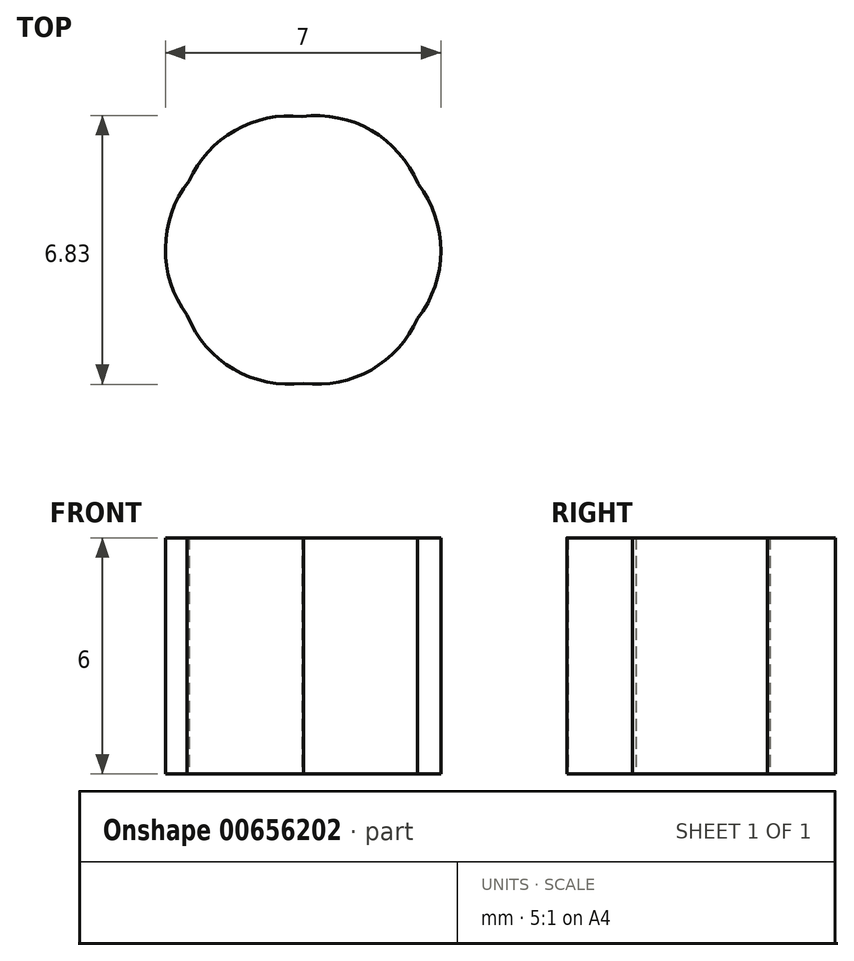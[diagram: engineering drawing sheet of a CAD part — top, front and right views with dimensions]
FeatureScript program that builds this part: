
annotation { "Feature Type Name" : "Feature", "Feature Type Description" : "" }
export const myFeature = defineFeature(function(context is Context, id is Id, definition is map)
    precondition{}
    {
        {
            var Q0;
            Q0=qCreatedBy(makeId("Top.planeOp"),FACE);
            var sketch = newSketch(context, id + "F0", { "sketchPlane" : qUnion([Q0])});
            skCircle(sketch, "E0", {"center": v(0, 0) * mm, "radius": 3.5 * mm});
            skCircle(sketch, "E1", {"center": v(-0.34, 0.6) * mm, "radius": 2.8 * mm});
            skCircle(sketch, "E2", {"center": v(0.33, 0.62) * mm, "radius": 2.8 * mm});
            skCircle(sketch, "E3", {"center": v(0.7, -0.02) * mm, "radius": 2.8 * mm});
            skCircle(sketch, "E4", {"center": v(0.35, -0.6) * mm, "radius": 2.8 * mm});
            skCircle(sketch, "E5", {"center": v(-0.35, -0.6) * mm, "radius": 2.8 * mm});
            skCircle(sketch, "E6", {"center": v(-0.7, 0.02) * mm, "radius": 2.8 * mm});
            skSolve(sketch);
        }
        {
            var Q0;
            {var subQ5=sQuery(id+"F0.wireOp",EDGE,"E2");var subQ7=sQuery(id+"F0.wireOp",EDGE,"E1");var subQ8=makeQuery(id+"F0.imprint","INTERSECT",VERTEX,{"disambiguationData":[OD(1.0)],"derivedFrom":[subQ7,subQ5]});Q0=makeQuery(id+"F0.imprint","IMPRINT",FACE,{"disambiguationData":[TD([[makeQuery(id+"F0.imprint","IMPRINT",EDGE,{"disambiguationData":[TD([[subQ8,-1.0]])],"derivedFrom":subQ7}),1.0]])]});}
            var Q1;
            {var subQ0=sQuery(id+"F0.wireOp",EDGE,"E5");var subQ1=sQuery(id+"F0.wireOp",EDGE,"E3");var subQ2=makeQuery(id+"F0.imprint","INTERSECT",VERTEX,{"disambiguationData":[OD(0.0)],"derivedFrom":[subQ1,subQ0]});Q1=makeQuery(id+"F0.imprint","IMPRINT",FACE,{"disambiguationData":[TD([[makeQuery(id+"F0.imprint","IMPRINT",EDGE,{"disambiguationData":[TD([[subQ2,-1.0]])],"derivedFrom":subQ1}),1.0]])]});}
            var Q2;
            {var subQ0=sQuery(id+"F0.wireOp",EDGE,"E6");var subQ1=sQuery(id+"F0.wireOp",EDGE,"E3");var subQ2=makeQuery(id+"F0.imprint","INTERSECT",VERTEX,{"disambiguationData":[OD(0.0)],"derivedFrom":[subQ1,subQ0]});Q2=makeQuery(id+"F0.imprint","IMPRINT",FACE,{"disambiguationData":[TD([[makeQuery(id+"F0.imprint","IMPRINT",EDGE,{"disambiguationData":[TD([[subQ2,-1.0]])],"derivedFrom":subQ1}),1.0]])]});}
            var Q3;
            {var subQ0=sQuery(id+"F0.wireOp",EDGE,"E6");var subQ1=sQuery(id+"F0.wireOp",EDGE,"E2");var subQ2=makeQuery(id+"F0.imprint","INTERSECT",VERTEX,{"disambiguationData":[OD(0.0)],"derivedFrom":[subQ1,subQ0]});Q3=makeQuery(id+"F0.imprint","IMPRINT",FACE,{"disambiguationData":[TD([[makeQuery(id+"F0.imprint","IMPRINT",EDGE,{"disambiguationData":[TD([[subQ2,-1.0]])],"derivedFrom":subQ1}),1.0]])]});}
            var Q4;
            {var subQ0=sQuery(id+"F0.wireOp",EDGE,"E5");var subQ1=sQuery(id+"F0.wireOp",EDGE,"E2");var subQ2=makeQuery(id+"F0.imprint","INTERSECT",VERTEX,{"disambiguationData":[OD(0.0)],"derivedFrom":[subQ1,subQ0]});Q4=makeQuery(id+"F0.imprint","IMPRINT",FACE,{"disambiguationData":[TD([[makeQuery(id+"F0.imprint","IMPRINT",EDGE,{"disambiguationData":[TD([[subQ2,-1.0]])],"derivedFrom":subQ1}),1.0]])]});}
            var Q5;
            {var subQ0=sQuery(id+"F0.wireOp",EDGE,"E4");var subQ1=sQuery(id+"F0.wireOp",EDGE,"E2");var subQ2=makeQuery(id+"F0.imprint","INTERSECT",VERTEX,{"disambiguationData":[OD(0.0)],"derivedFrom":[subQ1,subQ0]});Q5=makeQuery(id+"F0.imprint","IMPRINT",FACE,{"disambiguationData":[TD([[makeQuery(id+"F0.imprint","IMPRINT",EDGE,{"disambiguationData":[TD([[subQ2,-1.0]])],"derivedFrom":subQ1}),1.0]])]});}
            var Q6;
            {var subQ0=sQuery(id+"F0.wireOp",EDGE,"E5");var subQ1=sQuery(id+"F0.wireOp",EDGE,"E1");var subQ2=makeQuery(id+"F0.imprint","INTERSECT",VERTEX,{"disambiguationData":[OD(0.0)],"derivedFrom":[subQ1,subQ0]});Q6=makeQuery(id+"F0.imprint","IMPRINT",FACE,{"disambiguationData":[TD([[makeQuery(id+"F0.imprint","IMPRINT",EDGE,{"disambiguationData":[TD([[subQ2,-1.0]])],"derivedFrom":subQ1}),1.0]])]});}
            var Q7;
            {var subQ0=sQuery(id+"F0.wireOp",EDGE,"E6");var subQ1=sQuery(id+"F0.wireOp",EDGE,"E1");var subQ2=makeQuery(id+"F0.imprint","INTERSECT",VERTEX,{"disambiguationData":[OD(0.0)],"derivedFrom":[subQ1,subQ0]});Q7=makeQuery(id+"F0.imprint","IMPRINT",FACE,{"disambiguationData":[TD([[makeQuery(id+"F0.imprint","IMPRINT",EDGE,{"disambiguationData":[TD([[subQ2,-1.0]])],"derivedFrom":subQ1}),1.0]])]});}
            var Q8;
            {var subQ0=sQuery(id+"F0.wireOp",EDGE,"E3");var subQ1=sQuery(id+"F0.wireOp",EDGE,"E1");var subQ2=makeQuery(id+"F0.imprint","INTERSECT",VERTEX,{"disambiguationData":[OD(0.0)],"derivedFrom":[subQ1,subQ0]});Q8=makeQuery(id+"F0.imprint","IMPRINT",FACE,{"disambiguationData":[TD([[makeQuery(id+"F0.imprint","IMPRINT",EDGE,{"disambiguationData":[TD([[subQ2,-1.0]])],"derivedFrom":subQ1}),1.0]])]});}
            var Q9;
            {var subQ0=sQuery(id+"F0.wireOp",EDGE,"E3");var subQ1=sQuery(id+"F0.wireOp",EDGE,"E1");var subQ2=makeQuery(id+"F0.imprint","INTERSECT",VERTEX,{"disambiguationData":[OD(0.0)],"derivedFrom":[subQ1,subQ0]});Q9=makeQuery(id+"F0.imprint","IMPRINT",FACE,{"disambiguationData":[TD([[makeQuery(id+"F0.imprint","IMPRINT",EDGE,{"disambiguationData":[TD([[subQ2,-1.0]])],"derivedFrom":subQ1}),-1.0]])]});}
            var Q10;
            {var subQ0=sQuery(id+"F0.wireOp",EDGE,"E1");var subQ1=makeQuery(id+"F0.imprint","INTERSECT",VERTEX,{"derivedFrom":[sQuery(id+"F0.wireOp",EDGE,"E0"),subQ0]});Q10=makeQuery(id+"F0.imprint","IMPRINT",FACE,{"disambiguationData":[TD([[makeQuery(id+"F0.imprint","IMPRINT",EDGE,{"disambiguationData":[TD([[subQ1,1.0]])],"derivedFrom":subQ0}),1.0]])]});}
            var Q11;
            {var subQ0=sQuery(id+"F0.wireOp",EDGE,"E6");var subQ1=sQuery(id+"F0.wireOp",EDGE,"E4");var subQ2=makeQuery(id+"F0.imprint","INTERSECT",VERTEX,{"disambiguationData":[OD(0.0)],"derivedFrom":[subQ1,subQ0]});Q11=makeQuery(id+"F0.imprint","IMPRINT",FACE,{"disambiguationData":[TD([[makeQuery(id+"F0.imprint","IMPRINT",EDGE,{"disambiguationData":[TD([[subQ2,-1.0]])],"derivedFrom":subQ1}),1.0]])]});}
            var Q12;
            {var subQ0=sQuery(id+"F0.wireOp",EDGE,"E3");var subQ1=sQuery(id+"F0.wireOp",EDGE,"E1");var subQ2=makeQuery(id+"F0.imprint","INTERSECT",VERTEX,{"disambiguationData":[OD(0.0)],"derivedFrom":[subQ1,subQ0]});Q12=makeQuery(id+"F0.imprint","IMPRINT",FACE,{"disambiguationData":[TD([[makeQuery(id+"F0.imprint","IMPRINT",EDGE,{"disambiguationData":[TD([[subQ2,1.0]])],"derivedFrom":subQ1}),1.0]])]});}
            var Q13;
            {var subQ0=sQuery(id+"F0.wireOp",EDGE,"E3");var subQ1=sQuery(id+"F0.wireOp",EDGE,"E1");var subQ2=makeQuery(id+"F0.imprint","INTERSECT",VERTEX,{"disambiguationData":[OD(0.0)],"derivedFrom":[subQ1,subQ0]});Q13=makeQuery(id+"F0.imprint","IMPRINT",FACE,{"disambiguationData":[TD([[makeQuery(id+"F0.imprint","IMPRINT",EDGE,{"disambiguationData":[TD([[subQ2,1.0]])],"derivedFrom":subQ1}),-1.0]])]});}
            var Q14;
            {var subQ0=sQuery(id+"F0.wireOp",EDGE,"E3");var subQ1=sQuery(id+"F0.wireOp",EDGE,"E2");var subQ2=makeQuery(id+"F0.imprint","INTERSECT",VERTEX,{"disambiguationData":[OD(0.0)],"derivedFrom":[subQ1,subQ0]});Q14=makeQuery(id+"F0.imprint","IMPRINT",FACE,{"disambiguationData":[TD([[makeQuery(id+"F0.imprint","IMPRINT",EDGE,{"disambiguationData":[TD([[subQ2,1.0]])],"derivedFrom":subQ1}),-1.0]])]});}
            var Q15;
            {var subQ0=sQuery(id+"F0.wireOp",EDGE,"E4");var subQ1=sQuery(id+"F0.wireOp",EDGE,"E1");var subQ2=makeQuery(id+"F0.imprint","INTERSECT",VERTEX,{"disambiguationData":[OD(0.0)],"derivedFrom":[subQ1,subQ0]});Q15=makeQuery(id+"F0.imprint","IMPRINT",FACE,{"disambiguationData":[TD([[makeQuery(id+"F0.imprint","IMPRINT",EDGE,{"disambiguationData":[TD([[subQ2,1.0]])],"derivedFrom":subQ1}),-1.0]])]});}
            var Q16;
            {var subQ0=sQuery(id+"F0.wireOp",EDGE,"E4");var subQ1=sQuery(id+"F0.wireOp",EDGE,"E1");var subQ2=makeQuery(id+"F0.imprint","INTERSECT",VERTEX,{"disambiguationData":[OD(0.0)],"derivedFrom":[subQ1,subQ0]});Q16=makeQuery(id+"F0.imprint","IMPRINT",FACE,{"disambiguationData":[TD([[makeQuery(id+"F0.imprint","IMPRINT",EDGE,{"disambiguationData":[TD([[subQ2,1.0]])],"derivedFrom":subQ1}),1.0]])]});}
            var Q17;
            {var subQ0=sQuery(id+"F0.wireOp",EDGE,"E6");var subQ1=sQuery(id+"F0.wireOp",EDGE,"E1");var subQ2=makeQuery(id+"F0.imprint","INTERSECT",VERTEX,{"disambiguationData":[OD(1.0)],"derivedFrom":[subQ1,subQ0]});Q17=makeQuery(id+"F0.imprint","IMPRINT",FACE,{"disambiguationData":[TD([[makeQuery(id+"F0.imprint","IMPRINT",EDGE,{"disambiguationData":[TD([[subQ2,-1.0]])],"derivedFrom":subQ1}),1.0]])]});}
            var Q18;
            {var subQ0=sQuery(id+"F0.wireOp",EDGE,"E6");var subQ1=sQuery(id+"F0.wireOp",EDGE,"E1");var subQ2=makeQuery(id+"F0.imprint","INTERSECT",VERTEX,{"disambiguationData":[OD(1.0)],"derivedFrom":[subQ1,subQ0]});Q18=makeQuery(id+"F0.imprint","IMPRINT",FACE,{"disambiguationData":[TD([[makeQuery(id+"F0.imprint","IMPRINT",EDGE,{"disambiguationData":[TD([[subQ2,-1.0]])],"derivedFrom":subQ1}),-1.0]])]});}
            var Q19;
            {var subQ0=sQuery(id+"F0.wireOp",EDGE,"E5");var subQ1=sQuery(id+"F0.wireOp",EDGE,"E2");var subQ2=makeQuery(id+"F0.imprint","INTERSECT",VERTEX,{"disambiguationData":[OD(1.0)],"derivedFrom":[subQ1,subQ0]});Q19=makeQuery(id+"F0.imprint","IMPRINT",FACE,{"disambiguationData":[TD([[makeQuery(id+"F0.imprint","IMPRINT",EDGE,{"disambiguationData":[TD([[subQ2,-1.0]])],"derivedFrom":subQ1}),-1.0]])]});}
            var Q20;
            {var subQ0=sQuery(id+"F0.wireOp",EDGE,"E5");var subQ1=sQuery(id+"F0.wireOp",EDGE,"E3");var subQ2=makeQuery(id+"F0.imprint","INTERSECT",VERTEX,{"disambiguationData":[OD(1.0)],"derivedFrom":[subQ1,subQ0]});Q20=makeQuery(id+"F0.imprint","IMPRINT",FACE,{"disambiguationData":[TD([[makeQuery(id+"F0.imprint","IMPRINT",EDGE,{"disambiguationData":[TD([[subQ2,-1.0]])],"derivedFrom":subQ1}),-1.0]])]});}
            var Q21;
            {var subQ0=sQuery(id+"F0.wireOp",EDGE,"E6");var subQ1=sQuery(id+"F0.wireOp",EDGE,"E2");var subQ2=makeQuery(id+"F0.imprint","INTERSECT",VERTEX,{"disambiguationData":[OD(1.0)],"derivedFrom":[subQ1,subQ0]});Q21=makeQuery(id+"F0.imprint","IMPRINT",FACE,{"disambiguationData":[TD([[makeQuery(id+"F0.imprint","IMPRINT",EDGE,{"disambiguationData":[TD([[subQ2,-1.0]])],"derivedFrom":subQ1}),-1.0]])]});}
            var Q22;
            {var subQ0=sQuery(id+"F0.wireOp",EDGE,"E2");var subQ1=sQuery(id+"F0.wireOp",EDGE,"E1");var subQ2=makeQuery(id+"F0.imprint","INTERSECT",VERTEX,{"disambiguationData":[OD(1.0)],"derivedFrom":[subQ1,subQ0]});Q22=makeQuery(id+"F0.imprint","IMPRINT",FACE,{"disambiguationData":[TD([[makeQuery(id+"F0.imprint","IMPRINT",EDGE,{"disambiguationData":[TD([[subQ2,-1.0]])],"derivedFrom":subQ1}),-1.0]])]});}
            var Q23;
            {var subQ0=sQuery(id+"F0.wireOp",EDGE,"E3");var subQ1=sQuery(id+"F0.wireOp",EDGE,"E1");var subQ2=makeQuery(id+"F0.imprint","INTERSECT",VERTEX,{"disambiguationData":[OD(1.0)],"derivedFrom":[subQ1,subQ0]});Q23=makeQuery(id+"F0.imprint","IMPRINT",FACE,{"disambiguationData":[TD([[makeQuery(id+"F0.imprint","IMPRINT",EDGE,{"disambiguationData":[TD([[subQ2,-1.0]])],"derivedFrom":subQ1}),-1.0]])]});}
            var Q24;
            {var subQ0=sQuery(id+"F0.wireOp",EDGE,"E6");var subQ1=sQuery(id+"F0.wireOp",EDGE,"E3");var subQ2=makeQuery(id+"F0.imprint","INTERSECT",VERTEX,{"disambiguationData":[OD(1.0)],"derivedFrom":[subQ1,subQ0]});Q24=makeQuery(id+"F0.imprint","IMPRINT",FACE,{"disambiguationData":[TD([[makeQuery(id+"F0.imprint","IMPRINT",EDGE,{"disambiguationData":[TD([[subQ2,-1.0]])],"derivedFrom":subQ1}),-1.0]])]});}
            var Q25;
            {var subQ0=sQuery(id+"F0.wireOp",EDGE,"E4");var subQ1=sQuery(id+"F0.wireOp",EDGE,"E1");var subQ2=makeQuery(id+"F0.imprint","INTERSECT",VERTEX,{"disambiguationData":[OD(1.0)],"derivedFrom":[subQ1,subQ0]});Q25=makeQuery(id+"F0.imprint","IMPRINT",FACE,{"disambiguationData":[TD([[makeQuery(id+"F0.imprint","IMPRINT",EDGE,{"disambiguationData":[TD([[subQ2,-1.0]])],"derivedFrom":subQ1}),-1.0]])]});}
            var Q26;
            {var subQ0=sQuery(id+"F0.wireOp",EDGE,"E6");var subQ1=sQuery(id+"F0.wireOp",EDGE,"E4");var subQ2=makeQuery(id+"F0.imprint","INTERSECT",VERTEX,{"disambiguationData":[OD(1.0)],"derivedFrom":[subQ1,subQ0]});Q26=makeQuery(id+"F0.imprint","IMPRINT",FACE,{"disambiguationData":[TD([[makeQuery(id+"F0.imprint","IMPRINT",EDGE,{"disambiguationData":[TD([[subQ2,-1.0]])],"derivedFrom":subQ1}),-1.0]])]});}
            var Q27;
            {var subQ0=sQuery(id+"F0.wireOp",EDGE,"E3");var subQ1=sQuery(id+"F0.wireOp",EDGE,"E1");var subQ2=makeQuery(id+"F0.imprint","INTERSECT",VERTEX,{"disambiguationData":[OD(1.0)],"derivedFrom":[subQ1,subQ0]});Q27=makeQuery(id+"F0.imprint","IMPRINT",FACE,{"disambiguationData":[TD([[makeQuery(id+"F0.imprint","IMPRINT",EDGE,{"disambiguationData":[TD([[subQ2,-1.0]])],"derivedFrom":subQ1}),1.0]])]});}
            var Q28;
            {var subQ0=sQuery(id+"F0.wireOp",EDGE,"E4");var subQ1=sQuery(id+"F0.wireOp",EDGE,"E1");var subQ2=makeQuery(id+"F0.imprint","INTERSECT",VERTEX,{"disambiguationData":[OD(1.0)],"derivedFrom":[subQ1,subQ0]});Q28=makeQuery(id+"F0.imprint","IMPRINT",FACE,{"disambiguationData":[TD([[makeQuery(id+"F0.imprint","IMPRINT",EDGE,{"disambiguationData":[TD([[subQ2,-1.0]])],"derivedFrom":subQ1}),1.0]])]});}
            var Q29;
            {var subQ0=sQuery(id+"F0.wireOp",EDGE,"E5");var subQ1=sQuery(id+"F0.wireOp",EDGE,"E1");var subQ2=makeQuery(id+"F0.imprint","INTERSECT",VERTEX,{"disambiguationData":[OD(0.0)],"derivedFrom":[subQ1,subQ0]});Q29=makeQuery(id+"F0.imprint","IMPRINT",FACE,{"disambiguationData":[TD([[makeQuery(id+"F0.imprint","IMPRINT",EDGE,{"disambiguationData":[TD([[subQ2,-1.0]])],"derivedFrom":subQ1}),-1.0]])]});}
            var Q30;
            {var subQ0=sQuery(id+"F0.wireOp",EDGE,"E6");var subQ1=sQuery(id+"F0.wireOp",EDGE,"E1");var subQ2=makeQuery(id+"F0.imprint","INTERSECT",VERTEX,{"disambiguationData":[OD(0.0)],"derivedFrom":[subQ1,subQ0]});Q30=makeQuery(id+"F0.imprint","IMPRINT",FACE,{"disambiguationData":[TD([[makeQuery(id+"F0.imprint","IMPRINT",EDGE,{"disambiguationData":[TD([[subQ2,-1.0]])],"derivedFrom":subQ1}),-1.0]])]});}
            extrude(context, id + "F1", {"entities" : qUnion([Q0, Q1, Q2, Q3, Q4, Q5, Q6, Q7, Q8, Q9, Q10, Q11, Q12, Q13, Q14, Q15, Q16, Q17, Q18, Q19, Q20, Q21, Q22, Q23, Q24, Q25, Q26, Q27, Q28, Q29, Q30]), "depth" : 6 * mm, "offsetDistance" : 25 * mm});
        }
    });
